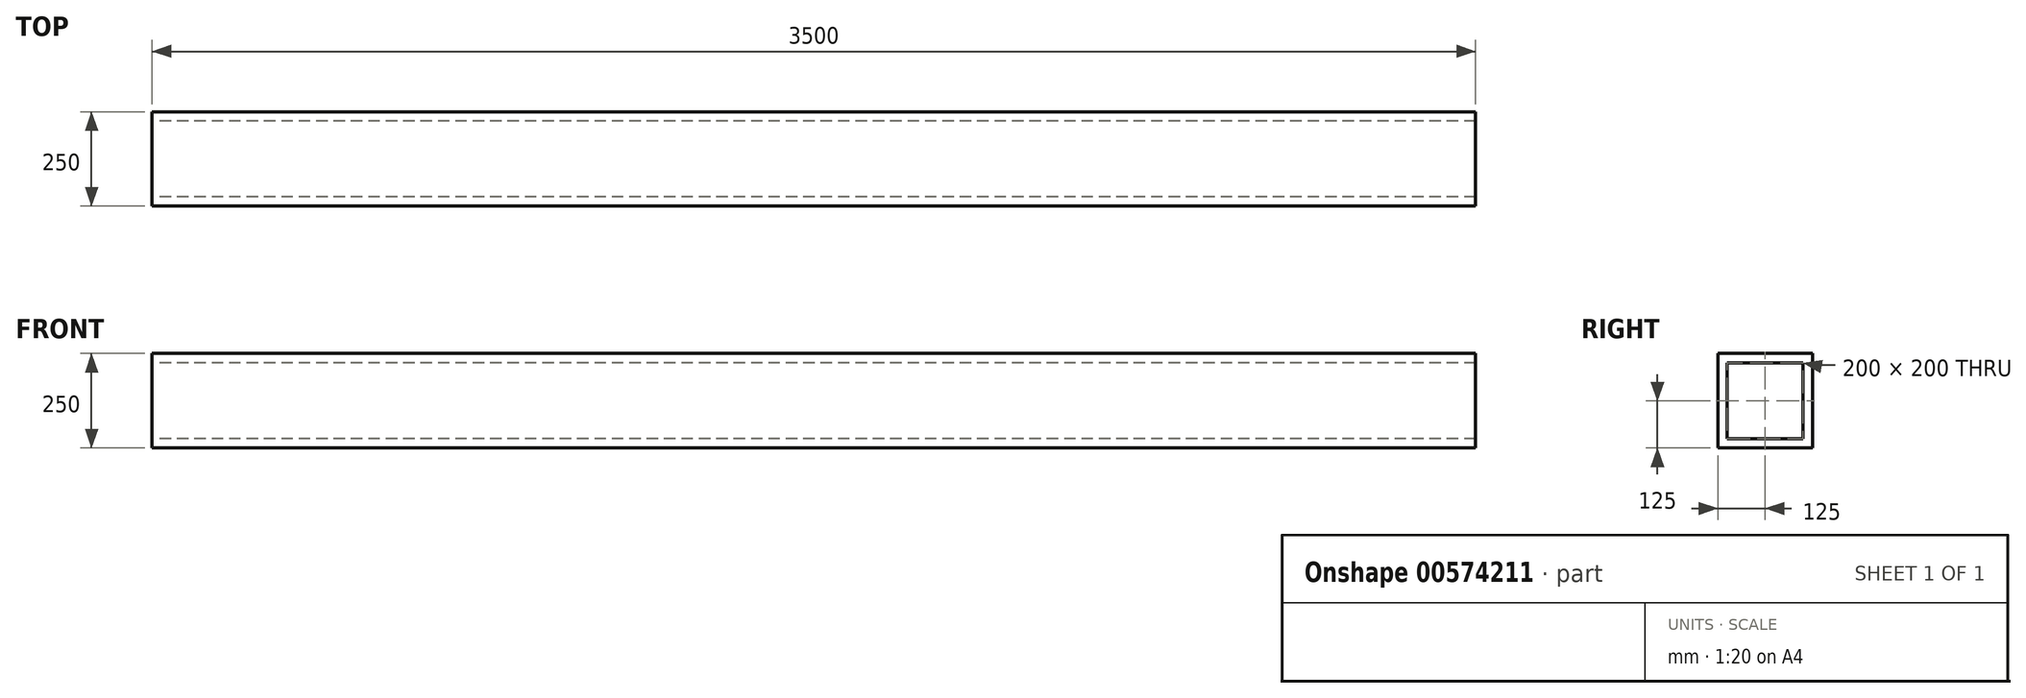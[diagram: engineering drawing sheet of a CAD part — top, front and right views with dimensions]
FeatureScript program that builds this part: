
annotation { "Feature Type Name" : "Feature", "Feature Type Description" : "" }
export const myFeature = defineFeature(function(context is Context, id is Id, definition is map)
    precondition{}
    {
        {
            var Q0;
            Q0=qCreatedBy(makeId("Right.planeOp"),FACE);
            var sketch = newSketch(context, id + "F0", { "sketchPlane" : qUnion([Q0])});
            skLineSegment(sketch, "E0.bottom", {"start": v(0, 0) * mm, "end": v(250, 0) * mm});
            skLineSegment(sketch, "E0.top", {"start": v(0, 250) * mm, "end": v(250, 250) * mm});
            skLineSegment(sketch, "E0.left", {"start": v(0, 0) * mm, "end": v(0, 250) * mm});
            skLineSegment(sketch, "E0.right", {"start": v(250, 0) * mm, "end": v(250, 250) * mm});
            skLineSegment(sketch, "E1.0", {"start": v(25, 225) * mm, "end": v(225, 225) * mm});
            skLineSegment(sketch, "E1.1", {"start": v(25, 25) * mm, "end": v(25, 225) * mm});
            skLineSegment(sketch, "E1.2", {"start": v(25, 25) * mm, "end": v(225, 25) * mm});
            skLineSegment(sketch, "E1.3", {"start": v(225, 25) * mm, "end": v(225, 225) * mm});
            skSolve(sketch);
        }
        {
            var Q0;
            Q0=makeQuery(id+"F0.imprint","IMPRINT",FACE,{"disambiguationData":[TD([[makeQuery(id+"F0.imprint","IMPRINT",EDGE,{"derivedFrom":sQuery(id+"F0.wireOp",EDGE,"E0.bottom")}),1.0]])]});
            extrude(context, id + "F1", {"entities" : qUnion([Q0]), "depth" : 3500 * mm, "offsetDistance" : 25 * mm});
        }
    });
